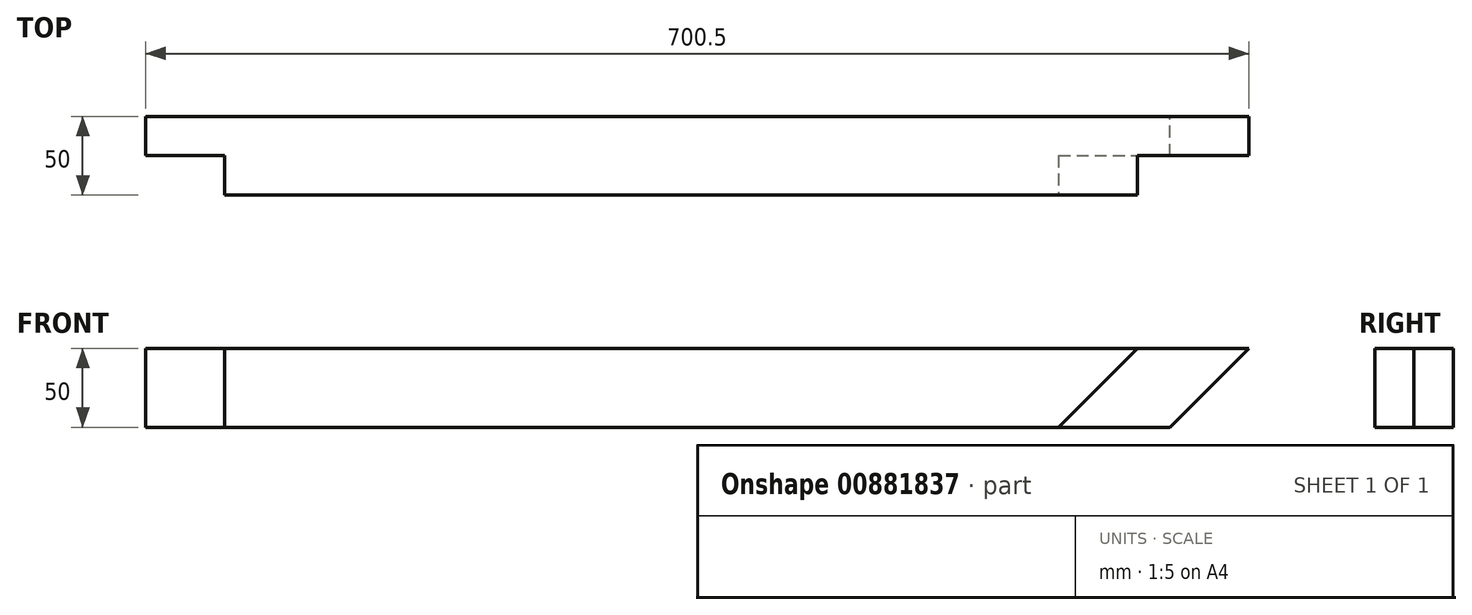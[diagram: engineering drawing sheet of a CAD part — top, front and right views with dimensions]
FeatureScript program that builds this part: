
annotation { "Feature Type Name" : "Feature", "Feature Type Description" : "" }
export const myFeature = defineFeature(function(context is Context, id is Id, definition is map)
    precondition{}
    {
        {
            var Q0;
            Q0=qCreatedBy(makeId("Front.planeOp"),FACE);
            var sketch = newSketch(context, id + "F0", { "sketchPlane" : qUnion([Q0])});
            skLineSegment(sketch, "E0", {"start": v(874.1, 24.7) * mm, "end": v(1524.6, 24.7) * mm});
            skLineSegment(sketch, "E1", {"start": v(1574.6, 74.7) * mm, "end": v(874.1, 74.7) * mm});
            skLineSegment(sketch, "E2", {"start": v(874.1, 74.7) * mm, "end": v(874.1, 24.7) * mm});
            skLineSegment(sketch, "E3.MirrorCS", {"start": v(1574.6, 74.7) * mm, "end": v(1524.6, 24.7) * mm});
            skSolve(sketch);
        }
        {
            var Q0;
            Q0=qSketchRegion(id+"F0",true);
            extrude(context, id + "F1", {"entities" : qUnion([Q0]), "depth" : 50 * mm, "offsetDistance" : 25 * mm});
        }
        {
            var Q0;
            Q0=makeQuery(id+"F1.opExtrude","CAP_FACE",FACE,{"disambiguationData":[OSD([sQuery(id+"F0.wireOp",EDGE,"E0"),sQuery(id+"F0.wireOp",EDGE,"E1"),sQuery(id+"F0.wireOp",EDGE,"E2"),sQuery(id+"F0.wireOp",EDGE,"qWGTyyMm-bhzb-qU72-nkJv-J7cF5fnZBEKZ")])],"isStart":false});
            var sketch = newSketch(context, id + "F2", { "sketchPlane" : qUnion([Q0])});
            skLineSegment(sketch, "E4", {"start": v(1574.6, 74.7) * mm, "end": v(1524.6, 24.7) * mm});
            skLineSegment(sketch, "E5", {"start": v(1524.6, 24.7) * mm, "end": v(1453.89, 24.7) * mm});
            skLineSegment(sketch, "E6", {"start": v(1453.89, 24.7) * mm, "end": v(1503.89, 74.7) * mm});
            skLineSegment(sketch, "E7", {"start": v(1503.89, 74.7) * mm, "end": v(1574.6, 74.7) * mm});
            skSolve(sketch);
        }
        {
            var Q0;
            Q0=qSketchRegion(id+"F2",true);
            extrude(context, id + "F3", {"entities" : qUnion([Q0]), "operationType" : NewBodyOperationType.REMOVE, "oppositeDirection" : true, "depth" : 25 * mm, "offsetDistance" : 25 * mm});
        }
        {
            var Q0;
            Q0=qSketchRegion(id+"F2",true);
            extrude(context, id + "F4", {"entities" : qUnion([Q0]), "operationType" : NewBodyOperationType.REMOVE, "oppositeDirection" : true, "depth" : 25 * mm, "offsetDistance" : 25 * mm});
        }
        {
            var Q0;
            Q0=makeQuery(id+"F1.opExtrude","CAP_FACE",FACE,{"disambiguationData":[OSD([sQuery(id+"F0.wireOp",EDGE,"E0"),sQuery(id+"F0.wireOp",EDGE,"E1"),sQuery(id+"F0.wireOp",EDGE,"E2"),sQuery(id+"F0.wireOp",EDGE,"E3.MirrorCS")])],"isStart":false});
            var sketch = newSketch(context, id + "F5", { "sketchPlane" : qUnion([Q0])});
            skLineSegment(sketch, "E8.bottom", {"start": v(874.1, 74.7) * mm, "end": v(924.1, 74.7) * mm});
            skLineSegment(sketch, "E8.top", {"start": v(874.1, 24.7) * mm, "end": v(924.1, 24.7) * mm});
            skLineSegment(sketch, "E8.left", {"start": v(874.1, 74.7) * mm, "end": v(874.1, 24.7) * mm});
            skLineSegment(sketch, "E8.right", {"start": v(924.1, 74.7) * mm, "end": v(924.1, 24.7) * mm});
            skSolve(sketch);
        }
        {
            var Q0;
            Q0 = qSketchRegion(id + "F5", true);
            extrude(context, id + "F6", {"entities" : qUnion([Q0]), "operationType" : NewBodyOperationType.REMOVE, "oppositeDirection" : true, "depth" : 25 * mm, "offsetDistance" : 25 * mm});
        }
    });
